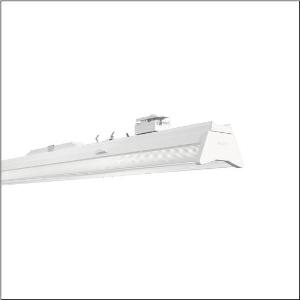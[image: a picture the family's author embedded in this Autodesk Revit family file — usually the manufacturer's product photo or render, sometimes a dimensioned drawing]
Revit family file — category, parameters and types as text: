
# Revit family: licross_r__11_performance_mo_51tm16mn4axg_6102
name_source: partatom
category: Lighting Fixtures
units: mm (PartAtom-declared; Revit-internal decimal feet)

## family parameters
Cut with Voids When Loaded = No
Host = Face
Light Source = No
Part Type = Normal
Room Calculation Point = No
Round Connector Dimension = Use Diameter
Shared = No

## types (1)
- --- (1 x LED, 10160 lm, 55.3 W, 4000K)
    Apparent Load = 55 VA
    CIE Flux Codes = 66 88 96 79 100
    Color Rendering = 80
    Color Temperature = 4000K
    Default Elevation = 1800 mm
    Description = Licross® 11 Performance MO, luminaire insert, of sheet steel, galvanised, coil coated, white, length: 1.500mm, width: 120mm, height: 123mm, LED rated luminous flux: 10.160lm, light colour: 840, control gear: ON/OFF Multilumen, with plug, 3-pole, with phase selection, mains connection: 220..240V, AC, 50/60Hz, rated input power: 55W, halogen-free wiring, primary light control with lens, of plastic, primary optical cover: cover, of PMMA, light emission: direct/indirect distribution, primary light characteristic: symmetric, protection rating (complete): IP40, insulation class (complete): insulation class I (protective earthing), certification: CE, ENEC, VDE, UKCA, protection symbol: D if used in an environment without relevant dust loads with corresponding accessories, impact resistance: IK06, permissible ambient temperature for indoor applications: -35..+40°C, corresponds to IFS (International Featured Standards) requirements for safety and quality in the food industry, reducing of maximum allowable ambient temperature of 5°C with ceiling mounting, LABS conformity tested according to VDMA 24364:2018-05, packaging unit: 1 piece
    Height = 114 mm
    Lamp = 1 x LED
    Lamp Light Flux = 10160 lm
    Lamp Power = 55.3 W
    Lamp count = 1
    Length = 1500 mm
    Luminous efficacy = 184 lm/W
    Manufacturer = Siteco
    ModVariant = No
    Model = 51TM16MN4AXG
    Mounting Place = Ceiling
    Mounting Type = Pendant
    Number of Poles = 1
    OnlyDefault = Yes
    Power Factor = 1
    Product Name = Licross® 11 Performance MO
    Product group = luminaire insert
    ProductGroupID = 901
    Protection Class = Protection class I
    Protection Degree = IP 40
    RLX_Detail_Level = 1
    RLX_Emergency_Light_Flux = 0 lm
    RLX_Emergency_Type = 0
    RLX_Emergency_Type_DB = No
    RlxData = <blob elided: 31801 chars, md5=a3321e6e>
    Socket = socket
    Standby Power = 0 W
    System Light Flux = 10160 lm
    System Power = 55 W
    Type Comments = factory setting: luminous flux: 100 % | (A | C | E) | 126 mA
    Type Image = l_1256138.jpg
    URL = http://relux.com
    VarID = @adj_038323
    Voltage = 0 V
    Weight = 0.00 kg
    Width = 120 mm

## geometry (parser evidence)
native form markers: Blend x4, Sweep x12
no freeform markers — native parametric forms only
